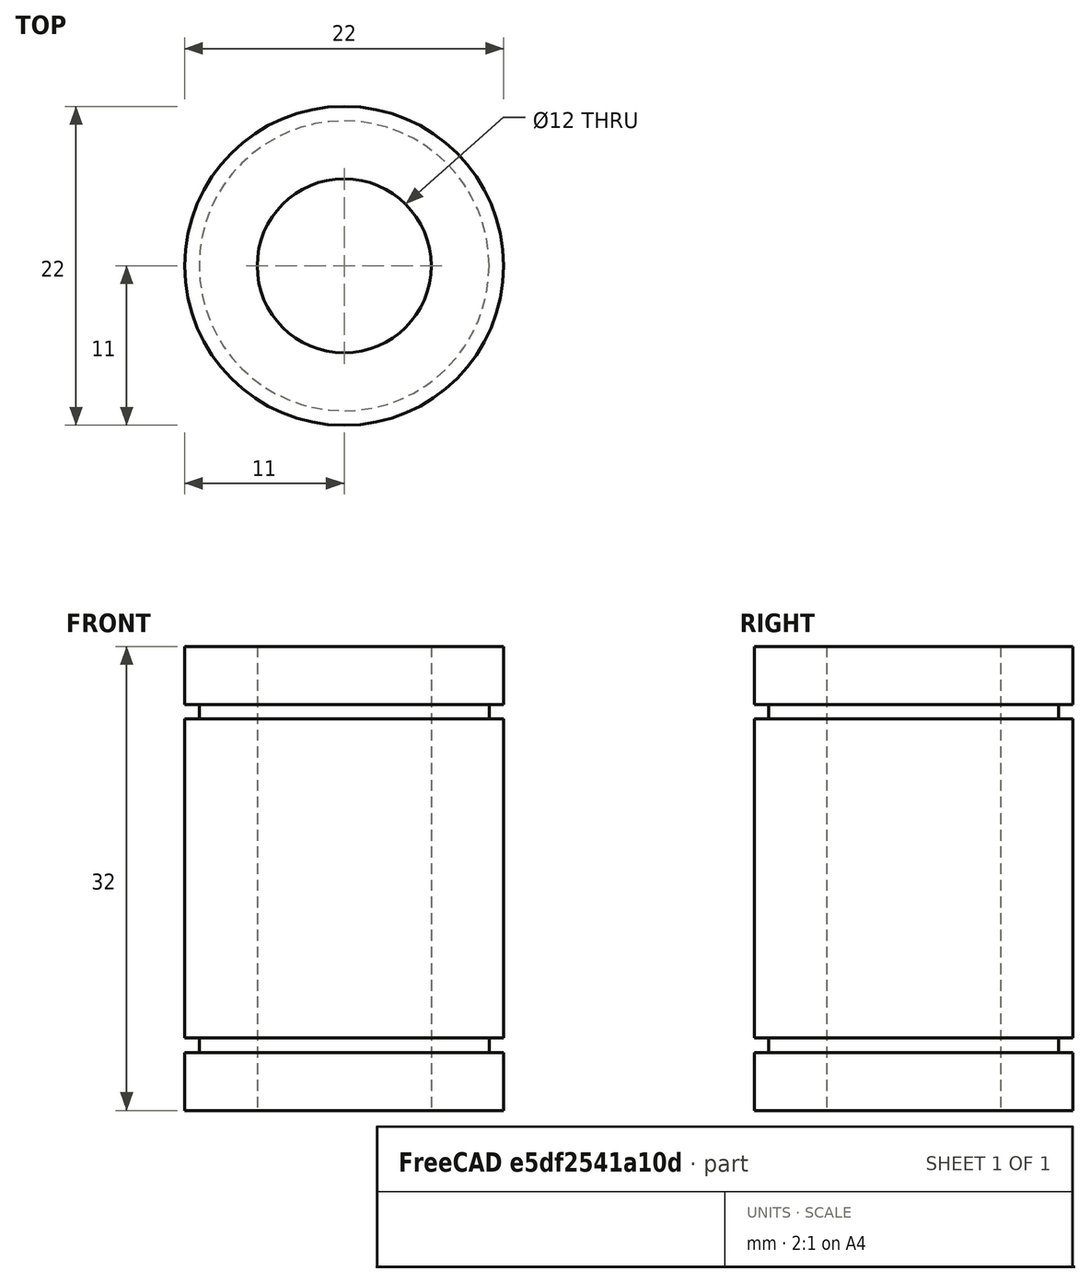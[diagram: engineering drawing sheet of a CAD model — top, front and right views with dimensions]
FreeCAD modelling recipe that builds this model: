
FCSTD DOCUMENT  (FreeCAD 0.15R4671 (Git))
Label: bearing
License: All rights reserved
LicenseURL: http://en.wikipedia.org/wiki/All_rights_reserved
objects: Sketcher::SketchObject×1, PartDesign::Revolution×1
note: 3 computed .brp shape members not serialized (recipe doc carries the construction recipe); baked Part::Feature solids carry a one-line shape summary decoded from their .brp

FEATURE [Sketcher::SketchObject] Sketch
  Placement = pos=(0,0,0) rot=(1,0,0;1.5708rad)
  sketch-geometry (14):
    g0: LineSegment StartX=6 StartY=16 StartZ=0 EndX=6 EndY=-16 EndZ=0
    g1: LineSegment StartX=6 StartY=-16 StartZ=0 EndX=11 EndY=-16 EndZ=0
    g2: LineSegment StartX=11 StartY=-16 StartZ=0 EndX=11 EndY=-12 EndZ=0
    g3: LineSegment StartX=11 StartY=-12 StartZ=0 EndX=10 EndY=-12 EndZ=0
    g4: LineSegment StartX=10 StartY=-12 StartZ=0 EndX=10 EndY=-11 EndZ=0
    g5: LineSegment StartX=10 StartY=-11 StartZ=0 EndX=11 EndY=-11 EndZ=0
    g6: LineSegment StartX=11 StartY=-11 StartZ=0 EndX=11 EndY=11 EndZ=0
    g7: LineSegment StartX=11 StartY=11 StartZ=0 EndX=10 EndY=11 EndZ=0
    g8: LineSegment StartX=10 StartY=11 StartZ=0 EndX=10 EndY=12 EndZ=0
    g9: LineSegment StartX=10 StartY=12 StartZ=0 EndX=11 EndY=12 EndZ=0
    g10: LineSegment StartX=11 StartY=12 StartZ=0 EndX=11 EndY=16 EndZ=0
    g11: LineSegment StartX=11 StartY=16 StartZ=0 EndX=6 EndY=16 EndZ=0
    g12: LineSegment [constr] StartX=0 StartY=0 StartZ=0 EndX=6 EndY=16 EndZ=0
    g13: LineSegment [constr] StartX=0 StartY=0 StartZ=0 EndX=6 EndY=-16 EndZ=0
  constraints (40):
    c: Vertical(g0)
    c: Coincident(g0,g1)
    c: Horizontal(g1)
    c: Coincident(g1,g2)
    c: Vertical(g2)
    c: Coincident(g2,g3)
    c: Horizontal(g3)
    c: Coincident(g3,g4)
    c: Vertical(g4)
    c: Coincident(g4,g5)
    c: Horizontal(g5)
    c: Coincident(g5,g6)
    c: Vertical(g6)
    c: Coincident(g6,g7)
    c: Horizontal(g7)
    c: Coincident(g7,g8)
    c: Vertical(g8)
    c: Coincident(g8,g9)
    c: Horizontal(g9)
    c: Coincident(g9,g10)
    c: Vertical(g10)
    c: Coincident(g10,g11)
    c: Coincident(g11,g0)
    c: Horizontal(g11)
    c: Equal(g2,g10)
    c: Equal(g8,g4)
    c: Equal(g9,g5)
    c: Coincident(g12,g-1)
    c: Coincident(g12,g0)
    c: Coincident(g13,g-1)
    c: Coincident(g13,g0)
    c: Equal(g12,g13)
    c: DistanceX(g0) = 6
    c: DistanceX(g10) = 11
    c: Equal(g9,g7)
    c: Equal(g3,g9)
    c: DistanceX(g9) = 1
    c: DistanceY(g8) = 1
    c: DistanceY(g7,g4) = -22
    c: DistanceY(g1,g10) = 32
FEATURE [PartDesign::Revolution] Revolution
  Angle = 360
  Axis = (0,0,1)
  Base = (0,0,0)
  Placement = pos=(0,0,0) rot=(1,0,0;1.5708rad)
  ReferenceAxis = -> Sketch [V_Axis]
  Sketch = -> Sketch
